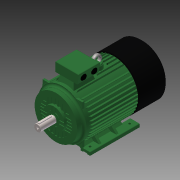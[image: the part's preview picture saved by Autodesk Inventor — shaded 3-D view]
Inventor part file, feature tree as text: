
AUTODESK INVENTOR PART (.ipt)
format: ipt  version: 2015 SP1 (Build 190203100, 203)  size: 1,014,784 bytes
history: native  units: in
note: dims shown in document units (in); Inventor stores cm internally (conversion verified against a paired STEP export)
features: other x3, imported_body x3, fillet x1
ambient origin geometry x8: Origin, YZ Plane, XZ Plane, XY Plane, X Axis, Y Axis, Z Axis, Center Point
bodies: Body1 (feature_tree), Body2 (feature_tree), Body3 (feature_tree)
feature tree (7):
  other  "Cut-Extrude3[1]"
  other  "TMDF 180L1"
  other  "Cut-Extrude3[2]"
  fillet  "Fillet3"  [1 undecoded]
  imported_body  "Base1"
  imported_body  "Base2"
  imported_body  "Base3"
note: 1 required parameter value undecoded (feature->parameter linkage not recoverable at this tier; creation-order binding heuristic only, values carry confidence <= 0.55)
